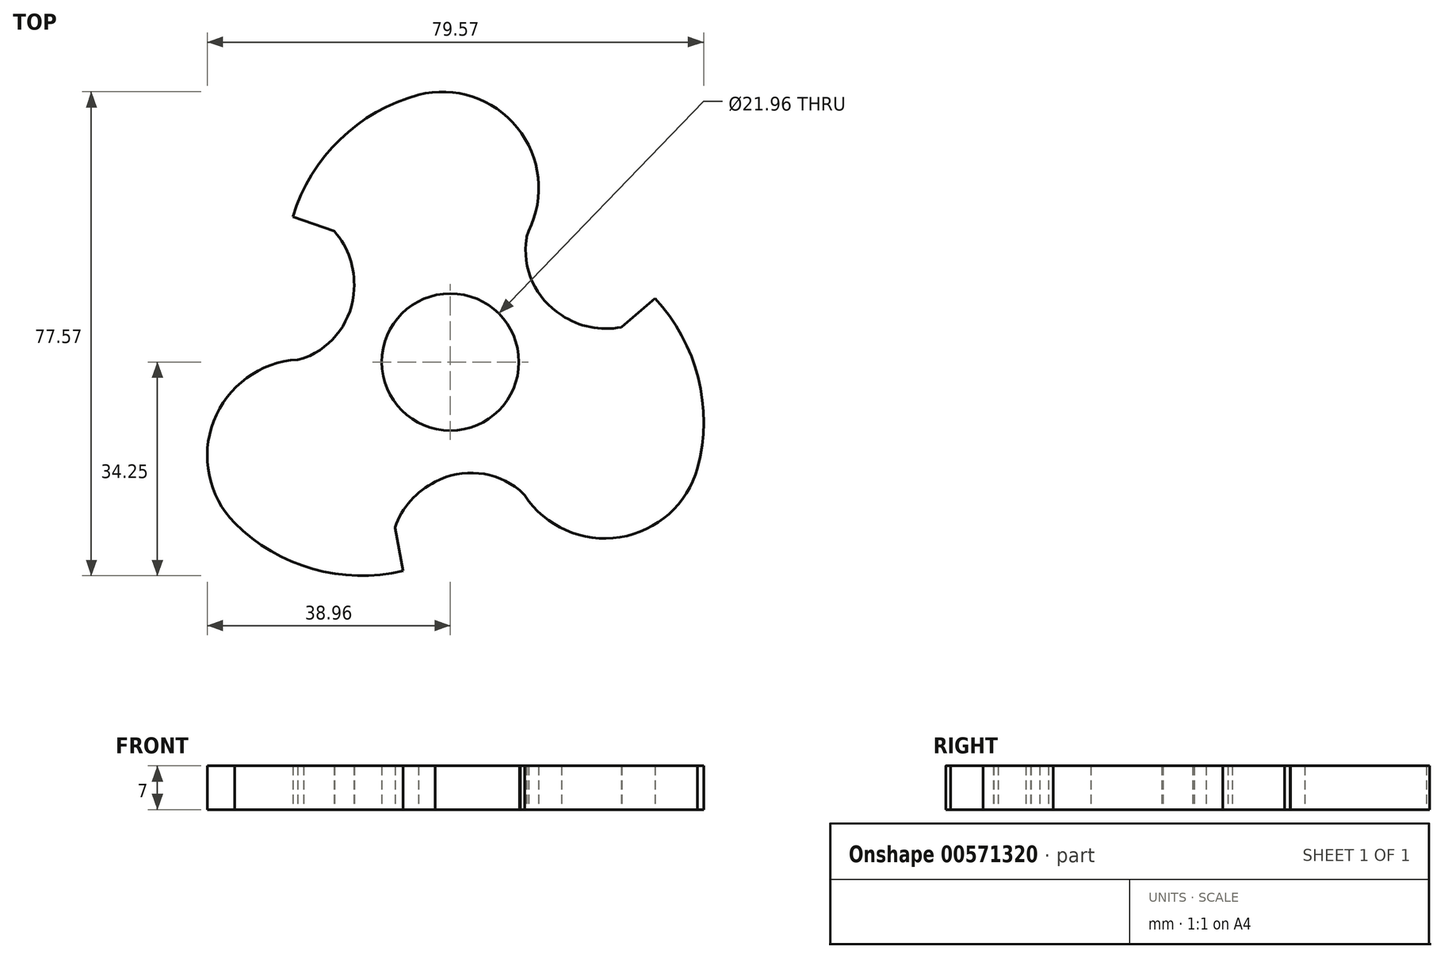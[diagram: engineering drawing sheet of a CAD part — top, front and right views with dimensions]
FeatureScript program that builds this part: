
annotation { "Feature Type Name" : "Feature", "Feature Type Description" : "" }
export const myFeature = defineFeature(function(context is Context, id is Id, definition is map)
    precondition{}
    {
        {
            var Q0;
            Q0=qCreatedBy(makeId("Top.planeOp"),FACE);
            var sketch = newSketch(context, id + "F0", { "sketchPlane" : qUnion([Q0])});
            skCircle(sketch, "E0", {"center": v(0, 0) * mm, "radius": 10.98 * mm});
            skPoint(sketch, "E1.start.orphan", {"position": v(0, 43.22) * mm});
            skPoint(sketch, "E2.2.0.end.orphan", {"position": v(32.77, 10.17) * mm});
            skPoint(sketch, "E3.orphan", {"position": v(11.11, -20.52) * mm});
            skPoint(sketch, "E4.trimOffspring.end.orphan", {"position": v(27.48, 5.59) * mm});
            skPoint(sketch, "E5.orphan", {"position": v(-8.9, -26.47) * mm});
            skPoint(sketch, "E6.orphan", {"position": v(-18.61, 21.02) * mm});
            skPoint(sketch, "E7.2.0", {"position": v(-23.33, 0.64) * mm});
            skArc(sketch, "E7.2.2", {"start": v(-23.36, 0.67) * mm, "mid": v(-17.74, 4.99) * mm, "end": v(-15.44, 11.7) * mm});
            skArc(sketch, "E7.2.3", {"start": v(-15.44, 11.7) * mm, "mid": v(-16.08, 16.63) * mm, "end": v(-18.56, 20.95) * mm});
            skLineSegment(sketch, "E7.2.4", {"start": v(-18.64, 21) * mm, "end": v(-25.23, 23.3) * mm});
            skLineSegment(sketch, "E7.2.5", {"start": v(-18.56, 20.95) * mm, "end": v(-18.64, 21) * mm});
            skArc(sketch, "E7.2.6", {"start": v(-5.1, 42.84) * mm, "mid": v(-17.7, 35.68) * mm, "end": v(-25.23, 23.3) * mm});
            skArc(sketch, "E7.2.7", {"start": v(12.54, 21) * mm, "mid": v(10.72, 37.58) * mm, "end": v(-5.1, 42.84) * mm});
            skPoint(sketch, "E8.orphan", {"position": v(12.77, 20.88) * mm});
            skPoint(sketch, "E9.1.3.end.orphan", {"position": v(-7.57, -33.47) * mm});
            skPoint(sketch, "E10.center", {"position": v(-0.02, -0.02) * mm});
            skPoint(sketch, "E11.orphan", {"position": v(12.23, 19.85) * mm});
            skPoint(sketch, "E12.orphan", {"position": v(32.77, 10.14) * mm});
            skLineSegment(sketch, "E13", {"start": v(-23.36, 0.67) * mm, "end": v(-23.52, 0.6) * mm});
            skPoint(sketch, "E14.orphan", {"position": v(-23.37, 0.63) * mm});
            skArc(sketch, "E15.1.2", {"start": v(11.1, -20.55) * mm, "mid": v(4.55, -17.84) * mm, "end": v(-2.4, -19.2) * mm});
            skArc(sketch, "E15.1.3", {"start": v(-2.4, -19.2) * mm, "mid": v(-6.36, -22.22) * mm, "end": v(-8.86, -26.52) * mm});
            skLineSegment(sketch, "E15.1.4", {"start": v(-8.87, -26.62) * mm, "end": v(-7.57, -33.48) * mm});
            skArc(sketch, "E15.1.5", {"start": v(-34.57, -25.8) * mm, "mid": v(-22.07, -33.15) * mm, "end": v(-7.57, -33.48) * mm});
            skArc(sketch, "E15.1.6", {"start": v(-24.49, 0.39) * mm, "mid": v(-37.93, -9.48) * mm, "end": v(-34.57, -25.8) * mm});
            skLineSegment(sketch, "E15.1.7", {"start": v(-24.49, 0.39) * mm, "end": v(-23.52, 0.6) * mm});
            skLineSegment(sketch, "E15.2.0", {"start": v(12.53, 20.98) * mm, "end": v(12.25, 20.09) * mm});
            skLineSegment(sketch, "E15.2.1", {"start": v(12.22, 19.9) * mm, "end": v(12.25, 20.09) * mm});
            skArc(sketch, "E15.2.2", {"start": v(12.22, 19.9) * mm, "mid": v(13.15, 12.87) * mm, "end": v(17.81, 7.52) * mm});
            skArc(sketch, "E15.2.3", {"start": v(17.81, 7.52) * mm, "mid": v(22.41, 5.6) * mm, "end": v(27.4, 5.59) * mm});
            skLineSegment(sketch, "E15.2.4", {"start": v(27.5, 5.63) * mm, "end": v(32.78, 10.18) * mm});
            skArc(sketch, "E15.2.5", {"start": v(39.63, -17.01) * mm, "mid": v(39.73, -2.53) * mm, "end": v(32.78, 10.18) * mm});
            skArc(sketch, "E15.2.6", {"start": v(11.9, -21.38) * mm, "mid": v(27.17, -28.09) * mm, "end": v(39.63, -17.01) * mm});
            skLineSegment(sketch, "E15.2.7", {"start": v(11.9, -21.38) * mm, "end": v(11.22, -20.63) * mm});
            skPoint(sketch, "E16.orphan", {"position": v(12.22, 19.89) * mm});
            skLineSegment(sketch, "E17", {"start": v(12.54, 21) * mm, "end": v(12.53, 20.98) * mm});
            skPoint(sketch, "E18.orphan", {"position": v(12.55, 21.05) * mm});
            skLineSegment(sketch, "E19", {"start": v(11.1, -20.55) * mm, "end": v(11.22, -20.63) * mm});
            skPoint(sketch, "E20.orphan", {"position": v(10.91, -20.39) * mm});
            skPoint(sketch, "E21.orphan", {"position": v(-23.11, 0.75) * mm});
            skPoint(sketch, "E22.orphan", {"position": v(-23.54, 0.6) * mm});
            skLineSegment(sketch, "E23", {"start": v(-8.86, -26.52) * mm, "end": v(-8.87, -26.62) * mm});
            skLineSegment(sketch, "E24", {"start": v(27.4, 5.59) * mm, "end": v(27.5, 5.63) * mm});
            skSolve(sketch);
        }
        {
            var Q0;
            Q0=qSketchRegion(id+"F0",true);
            extrude(context, id + "F1", {"entities" : qUnion([Q0]), "depth" : 7 * mm, "offsetDistance" : 25 * mm});
        }
    });
